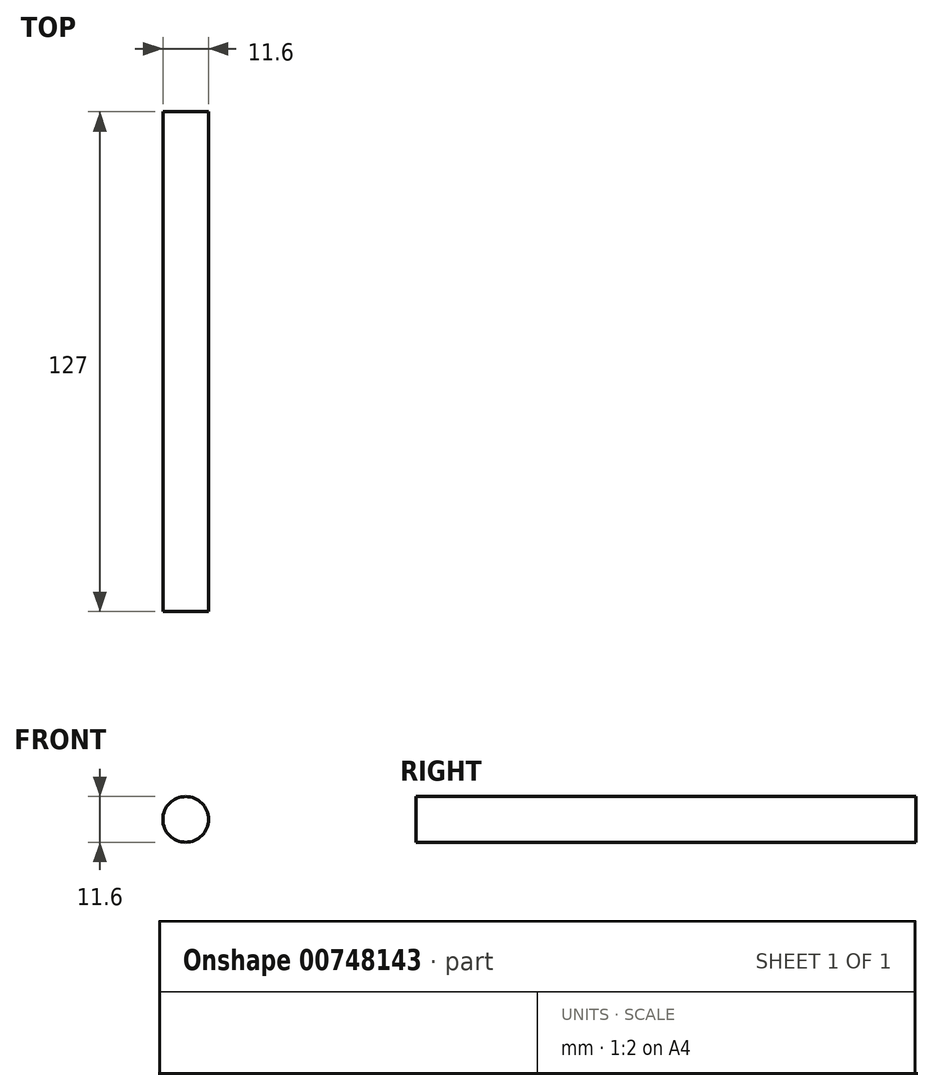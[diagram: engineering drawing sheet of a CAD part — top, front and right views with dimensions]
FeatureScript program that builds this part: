
annotation { "Feature Type Name" : "Feature", "Feature Type Description" : "" }
export const myFeature = defineFeature(function(context is Context, id is Id, definition is map)
    precondition{}
    {
        {
            var Q0;
            Q0=qCreatedBy(makeId("Front.planeOp"),FACE);
            var sketch = newSketch(context, id + "F0", { "sketchPlane" : qUnion([Q0])});
            skCircle(sketch, "E0", {"center": v(0, 0) * mm, "radius": 5.8 * mm});
            skSolve(sketch);
        }
        {
            var Q0;
            Q0=makeQuery(id+"F0.imprint","IMPRINT",FACE,{"disambiguationData":[TD([[makeQuery(id+"F0.imprint","IMPRINT",EDGE,{"derivedFrom":sQuery(id+"F0.wireOp",EDGE,"E0")}),1.0]])]});
            extrude(context, id + "F1", {"entities" : qUnion([Q0]), "depth" : 127 * mm, "offsetDistance" : 25.4 * mm});
        }
    });
